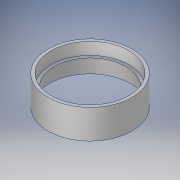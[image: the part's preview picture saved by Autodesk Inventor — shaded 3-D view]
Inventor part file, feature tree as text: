
AUTODESK INVENTOR PART (.ipt)
format: ipt  version: 2017 (Build 210142000, 142)  size: 157,696 bytes
history: native  units: in
note: dims shown in document units (in); Inventor stores cm internally (conversion verified against a paired STEP export)
features: revolve x1, sketch x1
ambient origin geometry x8: Origin, YZ Plane, XZ Plane, XY Plane, X Axis, Y Axis, Z Axis, Center Point
bodies: Solid1 (feature_tree)
feature tree (2):
  revolve  "Revolution1"  [1 undecoded]
  sketch  "Sketch1"  dims[d0=1.13in d1=3.7in d2=0.125in d3=0.1718in d5=1.0in d6=1.0in d7=90.0deg d8=0.5in d9=15.0deg d12=1.25in d13=0.25in d16=0.5in d17=0.5in d18=0.5in d19=2.5in d20=0.5in d22=0.375in d23=0.25in d25=0.234in d26=15.0deg d27=0.125in d28=0.25in d29=1.0in d30=4.25in d31=0.25in d32=1.0in d33=90.0deg]
note: 1 required parameter value undecoded (feature->parameter linkage not recoverable at this tier; creation-order binding heuristic only, values carry confidence <= 0.55)
